# Revit family: 3453A_NX_Network_Bridge_Module
name_source: partatom
category: Communication Devices
revit_build: Autodesk Revit 2014 (Build: 20130308_1515(x64)
units: mm (PartAtom-declared; Revit-internal decimal feet)

## types (1)
- 3453A_NX_Network_Bridge_Module
    Assembly Code = D5090
    Certificate = Title 24, c UL us
    Construction Housing = GSM UL Rated 94 HB Plastic
Plenum rated Complies with requirements for use in plenum
    Default Elevation = 48 "
    Description = The NX Network Bridge Module is a key component used in setting
up a NX Distributed Lighting Control Network comprised of NX Room
Controllers.
    Housing Material = Plastic - Hubbell - Blue
    Input = 50mA @12/24 volts DC, supplied by room controller SmartPort
    L = 5.26 "
    Manufacturer = Hubbell Control Solutions
    Model = NX Room Controller
    Mounting = Mounts directly to a junction box through an extended 1/2” chase nipple, mechanical only, no electrical connection
    Product Documentation Link = https://hubbellcdn.com
    Product Page URL = https://www.hubbell.com
    Type Comments = Network Bridge Module
    URL = https://www.hubbell.com
    Voltage = 12 V
    Warranty = 5-Years Warranty
    Washer = Metal-Hubbell-Galvanized_Steel

## geometry (parser evidence)
native form markers: Sweep x1
no freeform markers — native parametric forms only
